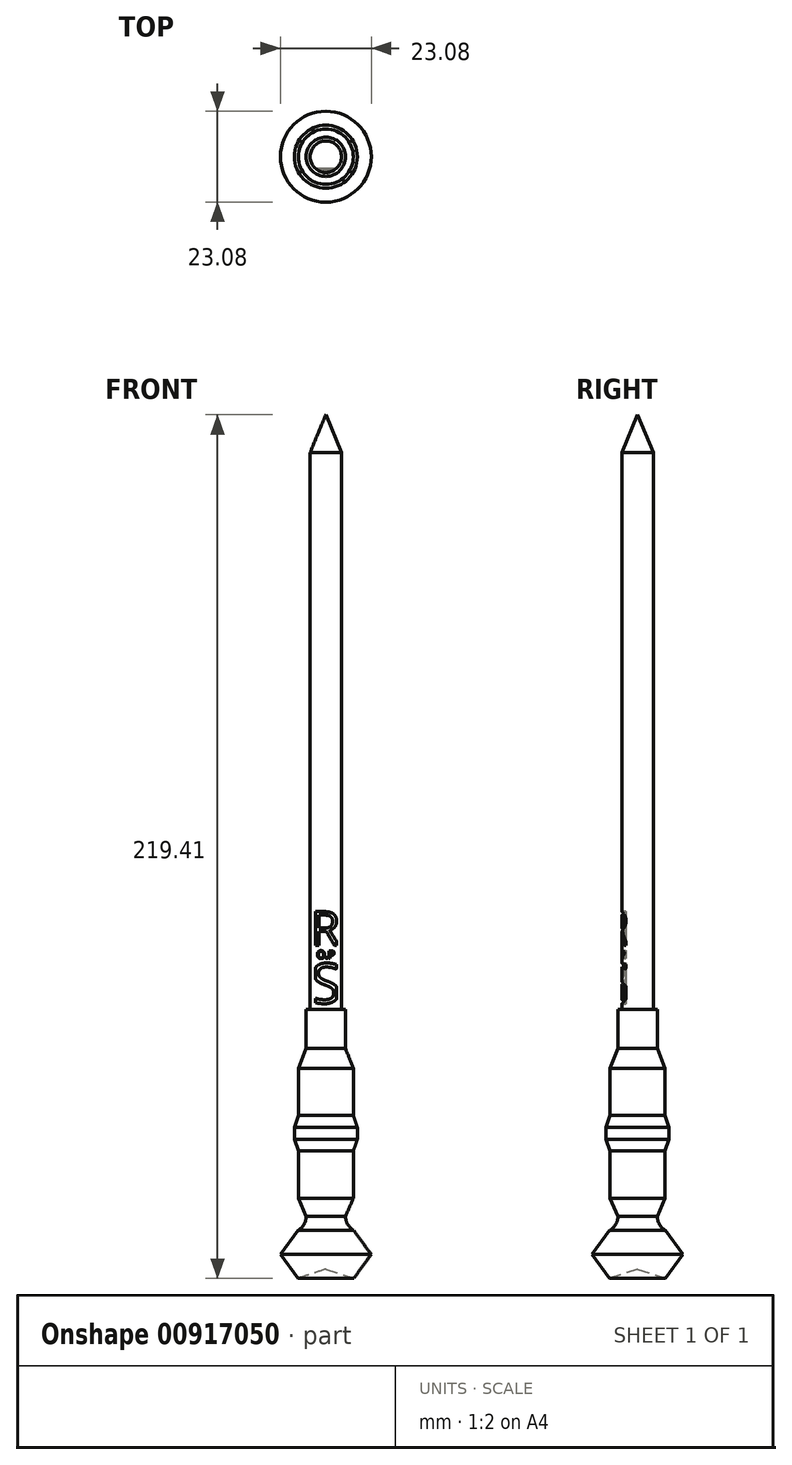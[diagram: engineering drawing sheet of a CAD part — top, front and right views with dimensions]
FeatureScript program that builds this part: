
annotation { "Feature Type Name" : "Feature", "Feature Type Description" : "" }
export const myFeature = defineFeature(function(context is Context, id is Id, definition is map)
    precondition{}
    {
        {
            var Q0;
            Q0=qCreatedBy(makeId("Front.planeOp"),FACE);
            var sketch = newSketch(context, id + "F0", { "sketchPlane" : qUnion([Q0])});
            skLineSegment(sketch, "E0", {"start": v(5, -107.92) * mm, "end": v(7, -103.34) * mm});
            skLineSegment(sketch, "E1", {"start": v(7, -103.34) * mm, "end": v(7, -91.34) * mm});
            skLineSegment(sketch, "E2", {"start": v(7, -91.34) * mm, "end": v(8, -88.34) * mm});
            skLineSegment(sketch, "E3", {"start": v(8, -88.34) * mm, "end": v(8, -85.34) * mm});
            skLineSegment(sketch, "E4", {"start": v(8, -85.34) * mm, "end": v(7, -82.34) * mm});
            skLineSegment(sketch, "E5", {"start": v(7, -82.34) * mm, "end": v(7, -70.34) * mm});
            skLineSegment(sketch, "E6", {"start": v(7, -70.34) * mm, "end": v(5, -65.34) * mm});
            skLineSegment(sketch, "E7", {"start": v(5, -65.34) * mm, "end": v(5, -55.34) * mm});
            skLineSegment(sketch, "E8", {"start": v(0, 86.13) * mm, "end": v(0, -113.87) * mm});
            skLineSegment(sketch, "E9", {"start": v(0, -113.87) * mm, "end": v(0, -121.37) * mm});
            skLineSegment(sketch, "E10", {"start": v(5, -107.92) * mm, "end": v(5, -107.92) * mm});
            skLineSegment(sketch, "E11", {"start": v(5, -55.34) * mm, "end": v(4, -55.34) * mm});
            skLineSegment(sketch, "E12", {"start": v(4, -55.34) * mm, "end": v(4, 86.13) * mm});
            skCircle(sketch, "E13.cCircle", {"center": v(5.16, -117.62) * mm, "radius": 6.38 * mm, "construction": true});
            skLineSegment(sketch, "E13.0", {"start": v(0, -113.87) * mm, "end": v(7.13, -111.55) * mm});
            skLineSegment(sketch, "E13.1", {"start": v(7.13, -111.55) * mm, "end": v(11.54, -117.62) * mm});
            skLineSegment(sketch, "E13.2", {"start": v(11.54, -117.62) * mm, "end": v(7.13, -123.68) * mm});
            skLineSegment(sketch, "E13.3", {"start": v(7.13, -123.68) * mm, "end": v(0, -121.37) * mm});
            skLineSegment(sketch, "E13.4", {"start": v(0, -121.37) * mm, "end": v(0, -113.87) * mm});
            skArc(sketch, "E14", {"start": v(5, -107.92) * mm, "mid": v(5.57, -110.02) * mm, "end": v(7.13, -111.55) * mm});
            skLineSegment(sketch, "E15", {"start": v(4, 86.13) * mm, "end": v(0, 95.73) * mm});
            skLineSegment(sketch, "E16", {"start": v(0, 95.73) * mm, "end": v(0, 86.13) * mm});
            skSolve(sketch);
        }
        {
            var Q0;
            {var subQ3=sQuery(id+"F0.wireOp",EDGE,"E1");Q0=makeQuery(id+"F0.imprint","IMPRINT",FACE,{"disambiguationData":[TD([[makeQuery(id+"F0.imprint","IMPRINT",EDGE,{"derivedFrom":subQ3}),1.0]])]});}
            var Q1;
            Q1=makeQuery(id+"F0.imprint","IMPRINT",FACE,{"disambiguationData":[TD([[makeQuery(id+"F0.imprint","IMPRINT",EDGE,{"derivedFrom":sQuery(id+"F0.wireOp",EDGE,"E9")}),1.0]])]});
            var Q2;
            {var subQ2=sQuery(id+"F0.wireOp",EDGE,"3RmAg1j2-Xwgd-ELF6-eAlD-LVp9lYji9hOZ");Q2=makeQuery(id+"F0.imprint","IMPRINT",FACE,{"disambiguationData":[TD([[makeQuery(id+"F0.imprint","IMPRINT",EDGE,{"derivedFrom":subQ2}),1.0]])]});}
            var Q3;
            {var subQ0=sQuery(id+"F0.wireOp",EDGE,"zJj0x5IR-v7HR-0kGa-kS1h-9tHZuanEryHu");Q3=makeQuery(id+"F0.imprint","IMPRINT",FACE,{"disambiguationData":[TD([[makeQuery(id+"F0.imprint","IMPRINT",EDGE,{"derivedFrom":subQ0}),-1.0]])]});}
            var Q4;
            {var subQ0=sQuery(id+"F0.wireOp",EDGE,"JNpCYwCD-FXzg-Cq6F-JqWC-qKrMH946LKzS");Q4=makeQuery(id+"F0.imprint","IMPRINT",FACE,{"disambiguationData":[TD([[makeQuery(id+"F0.imprint","IMPRINT",EDGE,{"derivedFrom":subQ0}),-1.0]])]});}
            var Q5;
            Q5=sQuery(id+"F0.wireOp",EDGE,"E8");
            revolve(context, id + "F1", {"surfaceOperationType" : NewSurfaceOperationType.NEW, "entities" : qUnion([Q0, Q1, Q2, Q3, Q4]), "axis" : qUnion([Q5]), "revolveType" : RevolveType.FULL});
        }
        {
            var Q0;
            Q0=qCreatedBy(makeId("Front.planeOp"),FACE);
            var sketch = newSketch(context, id + "F2", { "sketchPlane" : qUnion([Q0])});
            skText(sketch, "E17", { "text": "R", "fontName": "OpenSans-Regular.ttf"});
            skText(sketch, "E18", { "text": "S", "fontName": "OpenSans-Regular.ttf"});
            skText(sketch, "E19", { "text": "O.P", "fontName": "OpenSans-Regular.ttf"});
            const initialGuessF2  = {"E17": [-0.00389, -0.03911, 1, 0, 0.00865], "E18": [-0.00389, -0.0538, 1, 0, 0.01018], "E19": [-0.00232, -0.04244, 1, 0, 0.002]};
            skSetInitialGuess(sketch, initialGuessF2);
            skSolve(sketch);
        }
        {
            var Q0;
            Q0 = qSketchRegion(id + "F2", true);
            var Q1;
            Q1 = qConstructionFilter(qBodyType(qCreatedBy(id + "F2" ,EDGE), BodyType.WIRE), ConstructionObject.NO);
            extrude(context, id + "F3", {"entities" : qUnion([Q0]), "operationType" : NewBodyOperationType.REMOVE, "surfaceEntities" : qUnion([Q1]), "depth" : 10 * mm, "offsetDistance" : 25 * mm, "hasSecondDirection" : true, "secondDirectionOppositeDirection" : false, "secondDirectionDepth" : 3 * mm});
        }
    });
